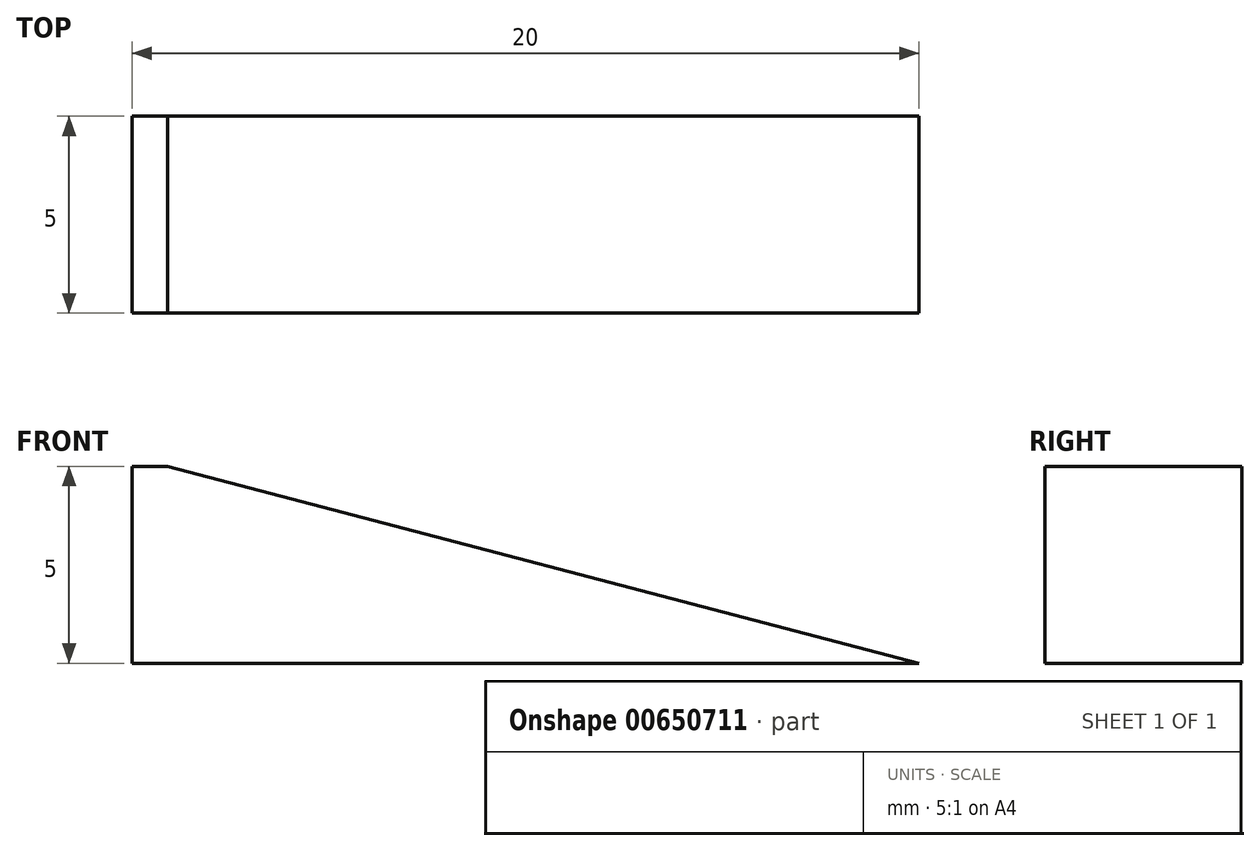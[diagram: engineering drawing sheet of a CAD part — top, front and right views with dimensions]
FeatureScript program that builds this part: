
annotation { "Feature Type Name" : "Feature", "Feature Type Description" : "" }
export const myFeature = defineFeature(function(context is Context, id is Id, definition is map)
    precondition{}
    {
        {
            var Q0;
            Q0=qCreatedBy(makeId("Top.planeOp"),FACE);
            var sketch = newSketch(context, id + "F0", { "sketchPlane" : qUnion([Q0])});
            skLineSegment(sketch, "E0.bottom", {"start": v(10, -2.5) * mm, "end": v(-10, -2.5) * mm});
            skLineSegment(sketch, "E0.top", {"start": v(10, 2.5) * mm, "end": v(-10, 2.5) * mm});
            skLineSegment(sketch, "E0.left", {"start": v(10, -2.5) * mm, "end": v(10, 2.5) * mm});
            skLineSegment(sketch, "E0.right", {"start": v(-10, -2.5) * mm, "end": v(-10, 2.5) * mm});
            skPoint(sketch, "E0.middle", {"position": v(0, 0) * mm});
            skSolve(sketch);
        }
        {
            var Q0;
            Q0 = qSketchRegion(id + "F0", true);
            var Q1;
            Q1=makeQuery(id+"F0.imprint","IMPRINT",FACE,{"disambiguationData":[TD([[makeQuery(id+"F0.imprint","IMPRINT",EDGE,{"derivedFrom":sQuery(id+"F0.wireOp",EDGE,"E0.bottom")}),-1.0]])]});
            extrude(context, id + "F1", {"entities" : qUnion([Q0, Q1]), "depth" : 5 * mm, "offsetDistance" : 25 * mm});
        }
        {
            var Q0;
            Q0=makeQuery(id+"F1.opExtrude","CAP_EDGE",EDGE,{"disambiguationData":[OSD([sQuery(id+"F0.wireOp",EDGE,"E0.left")])],"isStart":false});
            chamfer(context, id + "F2", {"entities" : qUnion([Q0]), "chamferType" : ChamferType.TWO_OFFSETS, "width1" : 19.1 * mm, "oppositeDirection" : false, "width2" : 5 * mm, "tangentPropagation" : true});
        }
    });
